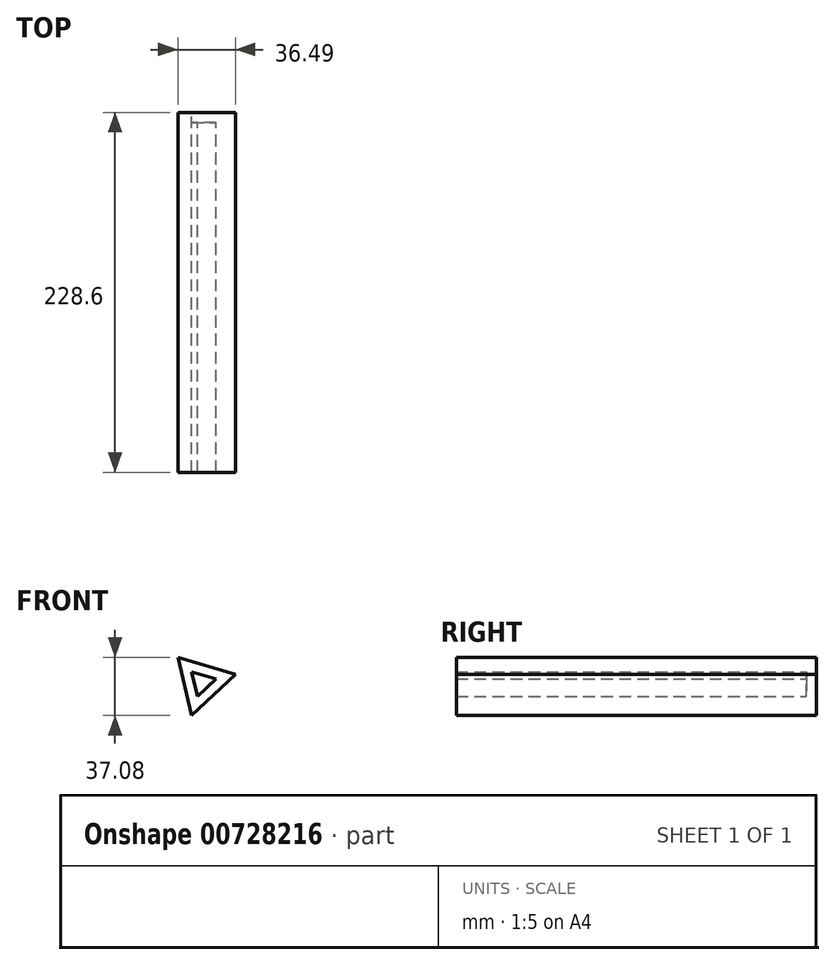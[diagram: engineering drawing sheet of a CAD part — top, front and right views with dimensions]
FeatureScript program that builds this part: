
annotation { "Feature Type Name" : "Feature", "Feature Type Description" : "" }
export const myFeature = defineFeature(function(context is Context, id is Id, definition is map)
    precondition{}
    {
        {
            var Q0;
            Q0=qCreatedBy(makeId("Front.planeOp"),FACE);
            var sketch = newSketch(context, id + "F0", { "sketchPlane" : qUnion([Q0])});
            skCircle(sketch, "E0.cCircle", {"center": v(0, 0) * mm, "radius": 11 * mm, "construction": true});
            skLineSegment(sketch, "E0.0", {"start": v(-15.08, 16.01) * mm, "end": v(21.4, 5.06) * mm});
            skLineSegment(sketch, "E0.1", {"start": v(21.4, 5.06) * mm, "end": v(-6.32, -21.07) * mm});
            skLineSegment(sketch, "E0.2", {"start": v(-6.32, -21.07) * mm, "end": v(-15.08, 16.01) * mm});
            skPoint(sketch, "E0.0.midPoint", {"position": v(3.16, 10.53) * mm});
            skSolve(sketch);
        }
        {
            var Q0;
            Q0=makeQuery(id+"F0.imprint","IMPRINT",FACE,{"disambiguationData":[TD([[makeQuery(id+"F0.imprint","IMPRINT",EDGE,{"derivedFrom":sQuery(id+"F0.wireOp",EDGE,"E0.0")}),-1.0]])]});
            extrude(context, id + "F1", {"entities" : qUnion([Q0]), "depth" : 228.6 * mm, "offsetDistance" : 25.4 * mm});
        }
        {
            var Q0;
            Q0=makeQuery(id+"F1.opExtrude","CAP_FACE",FACE,{"disambiguationData":[OSD([sQuery(id+"F0.wireOp",EDGE,"E0.0"),sQuery(id+"F0.wireOp",EDGE,"E0.1"),sQuery(id+"F0.wireOp",EDGE,"E0.2")])],"isStart":false});
            shell(context, id + "F2", {"entities" : qUnion([Q0]), "thickness" : 6.35 * mm});
        }
    });
